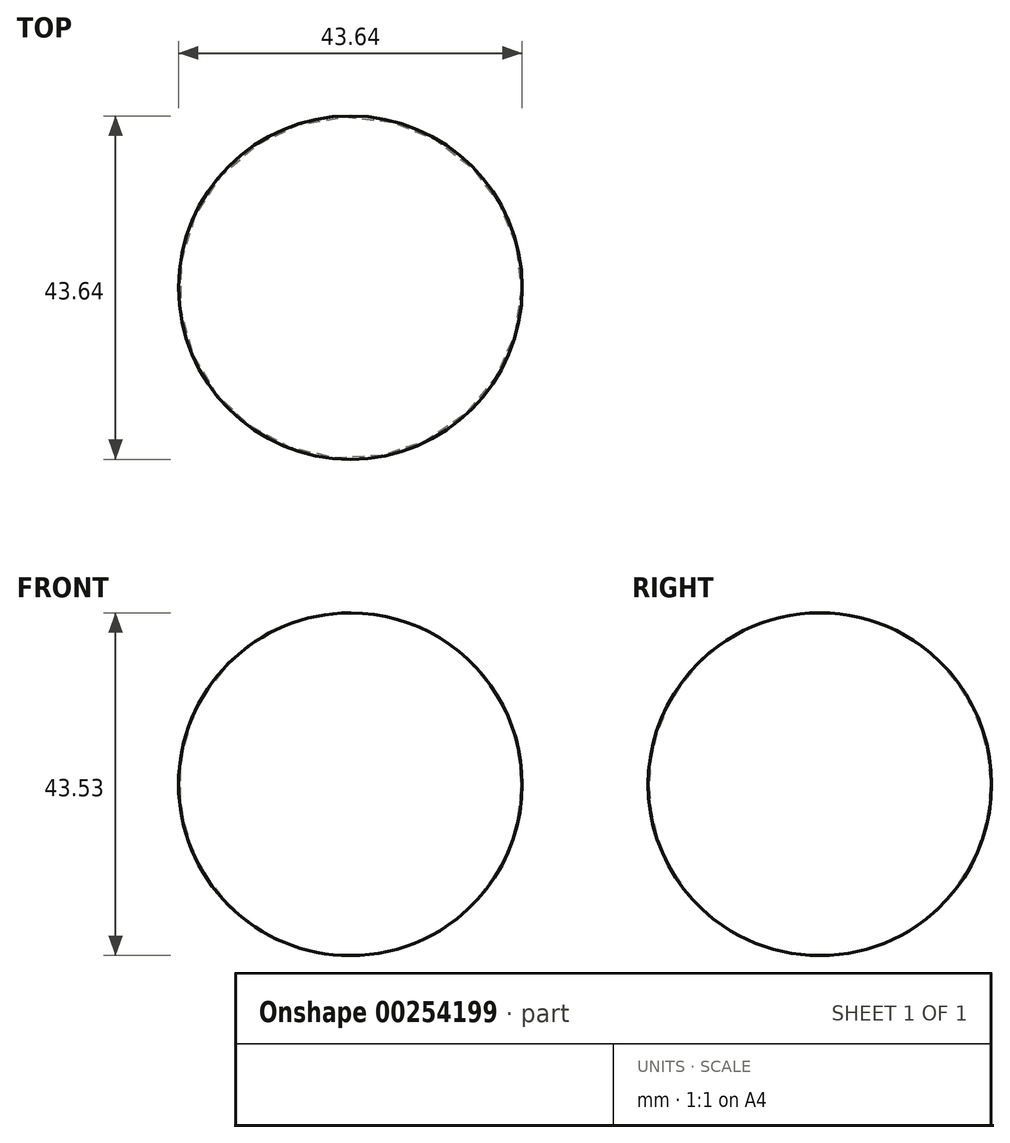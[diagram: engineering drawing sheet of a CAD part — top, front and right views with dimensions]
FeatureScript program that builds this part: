
annotation { "Feature Type Name" : "Feature", "Feature Type Description" : "" }
export const myFeature = defineFeature(function(context is Context, id is Id, definition is map)
    precondition{}
    {
        {
            var Q0;
            Q0=qCreatedBy(makeId("Front.planeOp"),FACE);
            var sketch = newSketch(context, id + "F0", { "sketchPlane" : qUnion([Q0])});
            skLineSegment(sketch, "E0", {"start": v(0, 0) * mm, "end": v(0, 43.53) * mm});
            skArc(sketch, "E1", {"start": v(0, 0) * mm, "mid": v(21.71, 21.77) * mm, "end": v(0, 43.53) * mm});
            skSolve(sketch);
        }
        {
            var Q0;
            Q0=makeQuery(id+"F0.imprint","IMPRINT",FACE,{"disambiguationData":[TD([[makeQuery(id+"F0.imprint","IMPRINT",EDGE,{"derivedFrom":sQuery(id+"F0.wireOp",EDGE,"E0")}),-1.0]])]});
            var Q1;
            Q1=sQuery(id+"F0.wireOp",EDGE,"E0");
            revolve(context, id + "F1", {"entities" : qUnion([Q0]), "axis" : qUnion([Q1]), "revolveType" : RevolveType.FULL});
        }
    });
